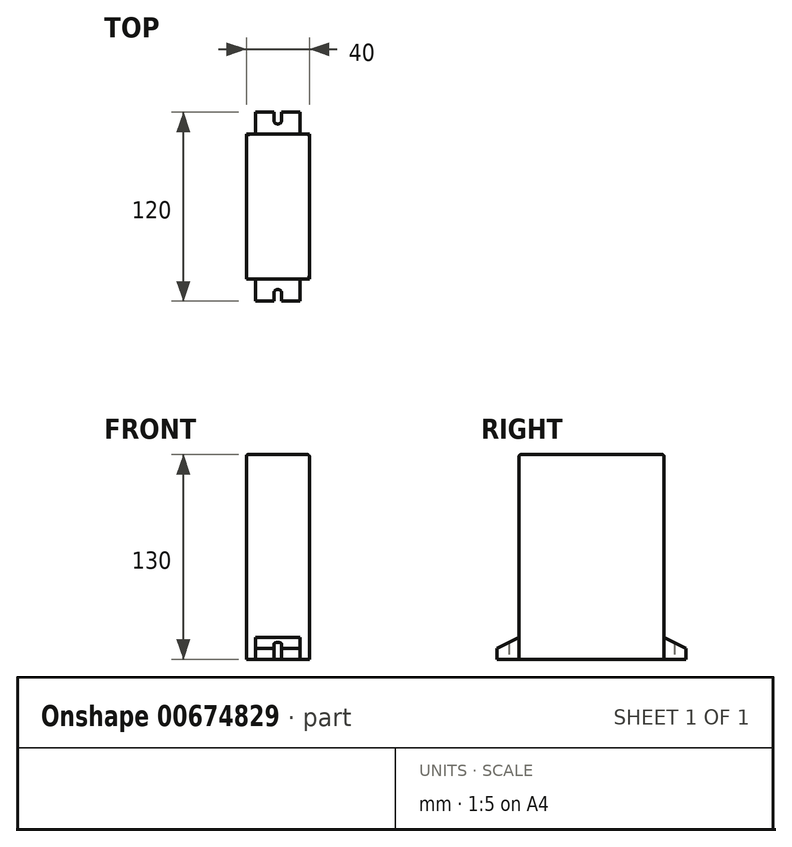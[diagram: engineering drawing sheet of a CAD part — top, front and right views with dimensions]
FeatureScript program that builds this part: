
annotation { "Feature Type Name" : "Feature", "Feature Type Description" : "" }
export const myFeature = defineFeature(function(context is Context, id is Id, definition is map)
    precondition{}
    {
        {
            var Q0;
            Q0=qCreatedBy(makeId("Right.planeOp"),FACE);
            var sketch = newSketch(context, id + "F0", { "sketchPlane" : qUnion([Q0])});
            skLineSegment(sketch, "E0.bottom", {"start": v(-67.77, 46) * mm, "end": v(62.23, 46) * mm});
            skLineSegment(sketch, "E0.top", {"start": v(-67.77, 0) * mm, "end": v(62.23, 0) * mm});
            skLineSegment(sketch, "E0.left", {"start": v(-67.77, 46) * mm, "end": v(-67.77, 0) * mm});
            skLineSegment(sketch, "E0.right", {"start": v(62.23, 46) * mm, "end": v(62.23, 0) * mm});
            skLineSegment(sketch, "E1.top", {"start": v(62.23, 60) * mm, "end": v(55.23, 60) * mm});
            skLineSegment(sketch, "E1.left", {"start": v(62.23, 46) * mm, "end": v(62.23, 60) * mm});
            skLineSegment(sketch, "E2", {"start": v(55.23, 60) * mm, "end": v(48.23, 46) * mm});
            skLineSegment(sketch, "E3.MirrorCS", {"start": v(-67.77, -46) * mm, "end": v(62.23, -46) * mm});
            skLineSegment(sketch, "E4.MirrorCS", {"start": v(62.23, -46) * mm, "end": v(62.23, 0) * mm});
            skLineSegment(sketch, "E5.MirrorCS", {"start": v(-67.77, -46) * mm, "end": v(-67.77, 0) * mm});
            skLineSegment(sketch, "E6.MirrorCS", {"start": v(55.23, -60) * mm, "end": v(48.23, -46) * mm});
            skLineSegment(sketch, "E7.MirrorCS", {"start": v(62.23, -60) * mm, "end": v(55.23, -60) * mm});
            skLineSegment(sketch, "E8.MirrorCS", {"start": v(62.23, -46) * mm, "end": v(62.23, -60) * mm});
            skSolve(sketch);
        }
        {
            var Q0;
            Q0=makeQuery(id+"F0.imprint","IMPRINT",FACE,{"disambiguationData":[TD([[makeQuery(id+"F0.imprint","IMPRINT",EDGE,{"derivedFrom":sQuery(id+"F0.wireOp",EDGE,"E0.top")}),1.0]])]});
            var Q1;
            Q1=makeQuery(id+"F0.imprint","IMPRINT",FACE,{"disambiguationData":[TD([[makeQuery(id+"F0.imprint","IMPRINT",EDGE,{"derivedFrom":sQuery(id+"F0.wireOp",EDGE,"E0.top")}),-1.0]])]});
            extrude(context, id + "F1", {"entities" : qUnion([Q0, Q1]), "depth" : 20 * mm, "offsetDistance" : 25 * mm, "hasSecondDirection" : true, "secondDirectionOppositeDirection" : true, "secondDirectionDepth" : 20 * mm});
        }
        {
            var Q0;
            Q0=makeQuery(id+"F0.imprint","IMPRINT",FACE,{"disambiguationData":[TD([[makeQuery(id+"F0.imprint","IMPRINT",EDGE,{"derivedFrom":sQuery(id+"F0.wireOp",EDGE,"E1.top")}),1.0]])]});
            var Q1;
            {var subQ2=sQuery(id+"F0.wireOp",EDGE,"E6.MirrorCS");Q1=makeQuery(id+"F0.imprint","IMPRINT",FACE,{"disambiguationData":[TD([[makeQuery(id+"F0.imprint","IMPRINT",EDGE,{"derivedFrom":subQ2}),-1.0]])]});}
            extrude(context, id + "F2", {"entities" : qUnion([Q0, Q1]), "operationType" : NewBodyOperationType.ADD, "depth" : 14 * mm, "offsetDistance" : 25 * mm, "hasSecondDirection" : true, "secondDirectionOppositeDirection" : true, "secondDirectionDepth" : 14 * mm});
        }
        {
            var Q0;
            Q0=makeQuery(id+"F2.boolean.opBoolean","MERGE",FACE,{"derivedFrom":[makeQuery(id+"F1.opExtrude","SWEPT_FACE",FACE,{"disambiguationData":[OSD([sQuery(id+"F0.wireOp",EDGE,"E0.right"),sQuery(id+"F0.wireOp",EDGE,"E4.MirrorCS")])]}),makeQuery(id+"F2.opExtrude","SWEPT_FACE",FACE,{"disambiguationData":[OSD([sQuery(id+"F0.wireOp",EDGE,"E1.left")])]}),makeQuery(id+"F2.opExtrude","SWEPT_FACE",FACE,{"disambiguationData":[OSD([sQuery(id+"F0.wireOp",EDGE,"E8.MirrorCS")])]})]});
            var sketch = newSketch(context, id + "F3", { "sketchPlane" : qUnion([Q0])});
            skArc(sketch, "E9", {"start": v(2.5, -55) * mm, "mid": v(0, -52.5) * mm, "end": v(-2.5, -55) * mm});
            skArc(sketch, "E10", {"start": v(-2.5, 55) * mm, "mid": v(0, 52.5) * mm, "end": v(2.5, 55) * mm});
            skLineSegment(sketch, "E11", {"start": v(2.5, 55) * mm, "end": v(2.5, 60) * mm});
            skLineSegment(sketch, "E12", {"start": v(-2.5, 55) * mm, "end": v(-2.5, 60) * mm});
            skLineSegment(sketch, "E13", {"start": v(2.5, -55) * mm, "end": v(2.5, -60) * mm});
            skLineSegment(sketch, "E14", {"start": v(-2.5, -55) * mm, "end": v(-2.5, -60) * mm});
            skSolve(sketch);
        }
        {
            var Q0;
            Q0=makeQuery(id+"F3.imprint","IMPRINT",FACE,{"disambiguationData":[TD([[makeQuery(id+"F3.imprint","IMPRINT",EDGE,{"derivedFrom":sQuery(id+"F3.wireOp",EDGE,"E10")}),1.0]])]});
            var Q1;
            Q1=makeQuery(id+"F3.imprint","IMPRINT",FACE,{"disambiguationData":[TD([[makeQuery(id+"F3.imprint","IMPRINT",EDGE,{"derivedFrom":sQuery(id+"F3.wireOp",EDGE,"E9")}),1.0]])]});
            extrude(context, id + "F4", {"entities" : qUnion([Q0, Q1]), "operationType" : NewBodyOperationType.REMOVE, "oppositeDirection" : true, "depth" : 25 * mm, "offsetDistance" : 25 * mm});
        }
        {
            var Q0;
            Q0=makeQuery(id+"F1.opExtrude","SWEPT_BODY",BODY,{"disambiguationData":[OSD([sQuery(id+"F0.wireOp",EDGE,"E0.bottom"),sQuery(id+"F0.wireOp",EDGE,"E0.left"),sQuery(id+"F0.wireOp",EDGE,"E0.right"),sQuery(id+"F0.wireOp",EDGE,"E3.MirrorCS"),sQuery(id+"F0.wireOp",EDGE,"E4.MirrorCS"),sQuery(id+"F0.wireOp",EDGE,"E5.MirrorCS")])]});
            var Q1;
            Q1=makeQuery(id+"F1.opExtrude","SWEPT_EDGE",EDGE,{"disambiguationData":[OSD([sQuery(id+"F0.wireOp",EDGE,"E0.bottom"),sQuery(id+"F0.wireOp",EDGE,"E0.left")])]});
            transform(context, id + "F5", {"entities" : qUnion([Q0]), "transformType" : TransformType.ROTATION, "transformAxis" : qUnion([Q1]), "angle" : 90 * degree, "makeCopy" : false});
        }
        {
            var Q0;
            Q0=makeQuery(id+"F1.opExtrude","SWEPT_EDGE",EDGE,{"disambiguationData":[OSD([sQuery(id+"F0.wireOp",EDGE,"E3.MirrorCS"),sQuery(id+"F0.wireOp",EDGE,"E5.MirrorCS")])]});
            var Q1;
            Q1=makeQuery(id+"F1.opExtrude","CAP_EDGE",EDGE,{"disambiguationData":[OSD([sQuery(id+"F0.wireOp",EDGE,"E0.left"),sQuery(id+"F0.wireOp",EDGE,"E5.MirrorCS")])],"isStart":false});
            var Q2;
            Q2=makeQuery(id+"F1.opExtrude","CAP_EDGE",EDGE,{"disambiguationData":[OSD([sQuery(id+"F0.wireOp",EDGE,"E0.left"),sQuery(id+"F0.wireOp",EDGE,"E5.MirrorCS")])],"isStart":true});
            var Q3;
            Q3=makeQuery(id+"F1.opExtrude","SWEPT_EDGE",EDGE,{"disambiguationData":[OSD([sQuery(id+"F0.wireOp",EDGE,"E0.bottom"),sQuery(id+"F0.wireOp",EDGE,"E0.left")])]});
            fillet(context, id + "F6", {"entities" : qUnion([Q0, Q1, Q2, Q3]), "radius" : 1 * mm, "tangentPropagation" : true, "allowEdgeOverflow" : false});
        }
    });
